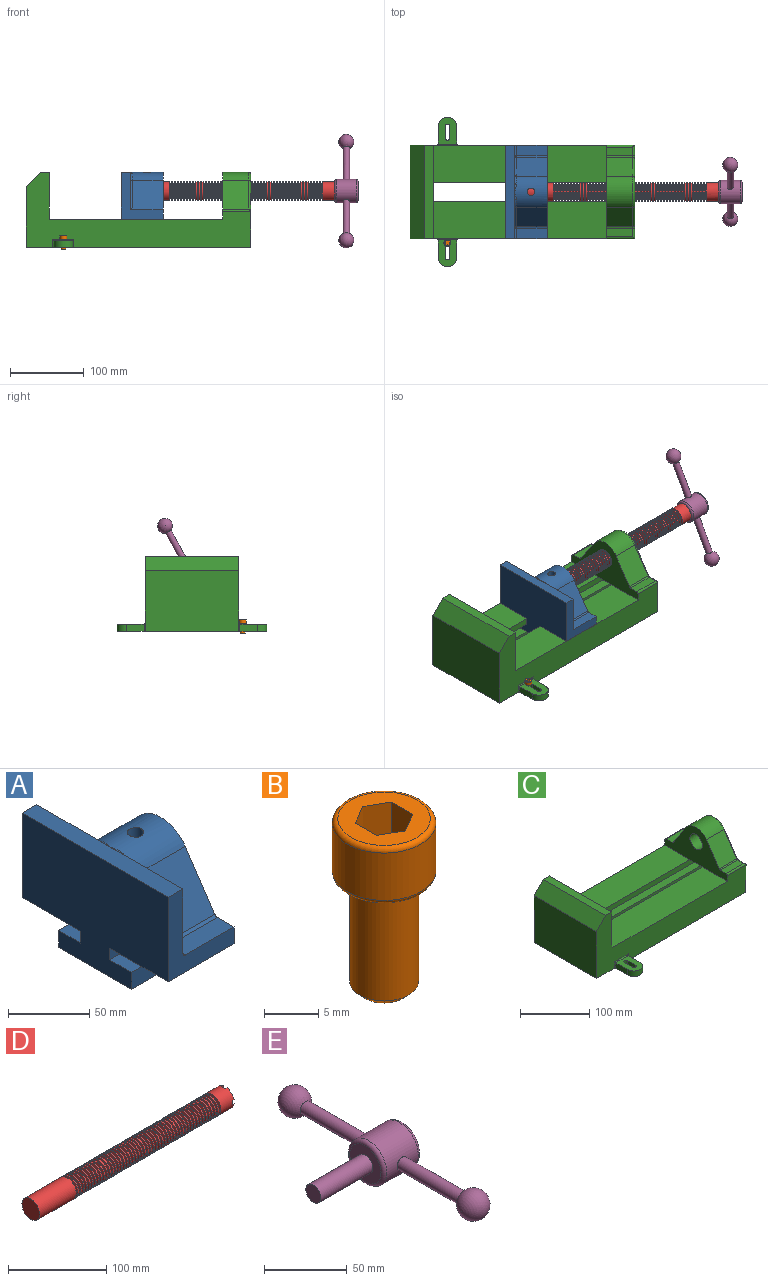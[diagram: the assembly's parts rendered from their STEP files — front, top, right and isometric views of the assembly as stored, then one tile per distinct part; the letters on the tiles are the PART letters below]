
ASSEMBLY  parts=5 mates=5
PART A: 36 faces, bbox 57.2x127x89 mm
  f0: plane 57.15x50.8mm, normal (0,0,-1), area 2903.2mm2, adj f6,f9,f10,f23
  f1: cylinder r=12.7mm len=44.45mm, axis (1,0,0), area 3464.3mm2, adj f6,f15,f16
  f2: plane 41.91x14.52mm, normal (0,0,1), area 608.5mm2, adj f6,f11,f24,f25
  f3: plane 51.86x48.26mm, normal (1,0,0), area 1495.7mm2, adj f8,f10,f31,f33,f35
  f4: plane 51.86x48.26mm, normal (1,0,0), area 1495.7mm2, adj f8,f11,f24,f28,f29
  f5: plane 57.15x50.8mm, normal (0,0,-1), area 2903.2mm2, adj f6,f9,f11,f22
  f6: plane 127x85.09mm, normal (1,0,0), area 5190.6mm2, adj f0,f1,f2,f5,f7,f10,f11,f12
  f7: plane 41.91x14.52mm, normal (0,0,1), area 608.5mm2, adj f6,f10,f30,f31
  f8: plane 127x12.7mm, normal (0,0,1), area 1612.9mm2, adj f3,f4,f9,f10,f11,f26,f34
  f9: plane 127x85.09mm, normal (-1,0,0), area 9096.8mm2, adj f0,f5,f8,f10,f11,f17,f18,f19
  f10: plane 63.5x57.15mm, normal (0,-1,0), area 1372.3mm2, adj f0,f3,f6,f7,f8,f9,f31
  f11: plane 63.5x57.15mm, normal (0,1,0), area 1372.3mm2, adj f2,f4,f5,f6,f8,f9,f24
  f12: plane 41.91x38.43mm, normal (0,-0.83,0.56), area 1939.2mm2, adj f6,f13,f30,f33
  f13: cylinder r=25.4mm len=44.45mm, axis (1,0,0), area 2026.5mm2, adj f6,f12,f14,f16,f26,f28,f34,f35
  f14: plane 41.91x38.43mm, normal (0,0.83,0.56), area 1939.2mm2, adj f6,f13,f25,f29
  f15: plane 25.4x25.4mm, normal (1,0,0), area 506.7mm2, adj f1
  f16: cylinder r=5.08mm len=13.76mm, axis (0,0,1), area 414mm2, adj f1,f13
  f17: plane 57.15x19.05mm, normal (0,0,1), area 1088.7mm2, adj f6,f9,f18,f23
  f18: plane 57.15x12.7mm, normal (0,-1,0), area 725.8mm2, adj f6,f9,f17,f19
  f19: plane 63.5x57.15mm, normal (0,0,-1), area 3629mm2, adj f6,f9,f18,f20
  f20: plane 57.15x12.7mm, normal (0,1,0), area 725.8mm2, adj f6,f9,f19,f21
  f21: plane 57.15x19.05mm, normal (0,0,1), area 1088.7mm2, adj f6,f9,f20,f22
  f22: plane 57.15x8.89mm, normal (0,1,0), area 508.1mm2, adj f5,f6,f9,f21
  f23: plane 57.15x8.89mm, normal (0,-1,0), area 508.1mm2, adj f0,f6,f9,f17
  f24: cylinder r=2.54mm len=14.52mm, axis (0,-1,0), area 57.9mm2, adj f2,f4,f11,f27
  f25: cylinder r=2.54mm len=41.91mm, axis (1,0,0), area 104.3mm2, adj f2,f6,f14,f27
  f26: bspline ~12.24x2.8mm, area 20.9mm2, adj f8,f13,f28
  f27: sphere r=2.54mm, area 6.3mm2, adj f24,f25,f29
  f28: torus R=27.94mm, axis (1,0,0), area 57.8mm2, adj f4,f13,f26,f29
  f29: cylinder r=2.54mm len=39.84mm, axis (0,-0.56,0.83), area 184.6mm2, adj f4,f14,f27,f28
  f30: cylinder r=2.54mm len=41.91mm, axis (1,0,0), area 104.3mm2, adj f6,f7,f12,f32
  f31: cylinder r=2.54mm len=14.52mm, axis (0,-1,0), area 57.9mm2, adj f3,f7,f10,f32
  f32: sphere r=2.54mm, area 6.3mm2, adj f30,f31,f33
  f33: cylinder r=2.54mm len=39.84mm, axis (0,-0.56,-0.83), area 184.6mm2, adj f3,f12,f32,f35
  f34: bspline ~12.24x2.8mm, area 20.9mm2, adj f8,f13,f35
  f35: torus R=27.94mm, axis (1,0,0), area 57.8mm2, adj f3,f13,f33,f34
PART B: 15 faces, bbox 10.3x10.3x19.1 mm
  f0: plane 8.51x8.51mm, normal (0,0,1), area 37.2mm2, adj f5,f6,f7,f8,f9,f10,f14
  f1: cylinder r=3.17mm len=11.94mm, axis (0,0,1), area 238.2mm2, adj f4,f12
  f2: plane 4.83x4.83mm, normal (0,0,-1), area 18.3mm2, adj f12
  f3: cylinder r=4.76mm len=9.53mm, axis (0,0,-1), area 159.6mm2, adj f13,f14
  f4: plane 8.51x8.51mm, normal (0,0,-1), area 25.2mm2, adj f1,f13
  f5: plane 4.83x2.38mm, normal (-0.5,-0.87,0), area 13.3mm2, adj f0,f6,f10,f11
  f6: plane 4.83x2.38mm, normal (0.5,-0.87,0), area 13.3mm2, adj f0,f5,f7,f11
  f7: plane 4.83x2.75mm, normal (1,0,0), area 13.3mm2, adj f0,f6,f8,f11
  f8: plane 4.83x2.38mm, normal (0.5,0.87,0), area 13.3mm2, adj f0,f7,f9,f11
  f9: plane 4.83x2.38mm, normal (-0.5,0.87,0), area 13.3mm2, adj f0,f8,f10,f11
  f10: plane 4.83x2.75mm, normal (-1,0,0), area 13.3mm2, adj f0,f5,f9,f11
  f11: plane 5.5x4.76mm, normal (0,0,1), area 19.6mm2, adj f5,f6,f7,f8,f9,f10
  f12: cone r=3.17mm half-angle=45deg, axis (0,0,1), area 18.9mm2, adj f1,f2
  f13: torus R=4.25mm, axis (0,0,1), area 23mm2, adj f3,f4
  f14: torus R=4.25mm, axis (0,0,1), area 23mm2, adj f0,f3
PART C: 61 faces, bbox 304.8x203.2x103.7 mm
  f0: plane 304.8x101.6mm, normal (0,1,0), area 13520.3mm2, adj f3,f4,f5,f6,f7,f8,f9,f16
  f1: plane 304.8x101.6mm, normal (0,-1,0), area 13520.3mm2, adj f2,f3,f5,f6,f7,f8,f9,f16
  f2: plane 234.95x50.8mm, normal (0,0,1), area 11935.5mm2, adj f1,f5,f16,f26
  f3: plane 127x99.06mm, normal (1,0,0), area 7097.5mm2, adj f0,f1,f9,f14,f17,f18,f19,f20
  f4: plane 234.95x50.8mm, normal (0,0,1), area 11935.5mm2, adj f0,f5,f16,f27
  f5: plane 127x101.6mm, normal (1,0,0), area 9516.1mm2, adj f0,f1,f2,f4,f6,f9,f18,f19
  f6: plane 127x12.7mm, normal (0,0,1), area 1612.9mm2, adj f0,f1,f5,f7
  f7: plane 127x19.05mm, normal (-0.71,0,0.71), area 3421.5mm2, adj f0,f1,f6,f8
  f8: plane 127x82.55mm, normal (-1,0,0), area 10483.8mm2, adj f0,f1,f7,f9
  f9: plane 304.8x203.2mm, normal (0,0,-1), area 33298.3mm2, adj f0,f1,f3,f5,f8,f21,f22,f39
  f10: plane 35.56x11.98mm, normal (0,0,1), area 426mm2, adj f16,f28,f29,f30
  f11: plane 38.43x35.56mm, normal (0,0.83,0.56), area 1645.4mm2, adj f12,f16,f29,f32
  f12: cylinder r=25.4mm len=42.19mm, axis (1,0,0), area 1770.2mm2, adj f11,f13,f16,f33
  f13: plane 38.43x35.56mm, normal (0,-0.83,0.56), area 1645.4mm2, adj f12,f16,f34,f35
  f14: cylinder r=12.7mm len=38.1mm, axis (1,0,0), area 3040.2mm2, adj f3,f16
  f15: plane 35.56x11.98mm, normal (0,0,1), area 426mm2, adj f16,f34,f36,f38
  f16: plane 127x63.5mm, normal (-1,0,0), area 4155.5mm2, adj f0,f1,f2,f4,f10,f11,f12,f13
  f17: plane 38.1x25.4mm, normal (0,0,-1), area 967.7mm2, adj f3,f16,f26,f27
  f18: plane 273.05x19.05mm, normal (0,0,-1), area 5201.6mm2, adj f3,f5,f19,f26
  f19: plane 273.05x12.7mm, normal (0,1,0), area 3467.7mm2, adj f3,f5,f18,f20
  f20: plane 273.05x19.05mm, normal (0,0,1), area 5201.6mm2, adj f3,f5,f19,f21
  f21: plane 273.05x16.51mm, normal (0,1,0), area 4508.1mm2, adj f3,f5,f9,f20
  f22: plane 273.05x16.51mm, normal (0,-1,0), area 4508.1mm2, adj f3,f5,f9,f23
  f23: plane 273.05x19.05mm, normal (0,0,1), area 5201.6mm2, adj f3,f5,f22,f24
  f24: plane 273.05x12.7mm, normal (0,-1,0), area 3467.7mm2, adj f3,f5,f23,f25
  f25: plane 273.05x19.05mm, normal (0,0,-1), area 5201.6mm2, adj f3,f5,f24,f27
  f26: plane 273.05x8.89mm, normal (0,1,0), area 2427.4mm2, adj f2,f3,f5,f17,f18
  f27: plane 273.05x8.89mm, normal (0,-1,0), area 2427.4mm2, adj f3,f4,f5,f17,f25
  f28: cylinder r=2.54mm len=38.1mm, axis (1,0,0), area 148.3mm2, adj f0,f10,f16,f30
  f29: cylinder r=2.54mm len=35.56mm, axis (-1,0,0), area 88.5mm2, adj f10,f11,f16,f31
  f30: cylinder r=2.54mm len=14.52mm, axis (0,1,0), area 54.3mm2, adj f3,f10,f28,f31
  f31: torus R=5.08mm, axis (-1,0,0), area 13.5mm2, adj f3,f29,f30,f32
  f32: cylinder r=2.54mm len=39.84mm, axis (0,0.56,-0.83), area 184.6mm2, adj f3,f11,f31,f33
  f33: torus R=22.86mm, axis (-1,0,0), area 191.4mm2, adj f3,f12,f32,f35
  f34: cylinder r=2.54mm len=35.56mm, axis (-1,0,0), area 88.5mm2, adj f13,f15,f16,f37
  f35: cylinder r=2.54mm len=39.84mm, axis (0,0.56,0.83), area 184.6mm2, adj f3,f13,f33,f37
  f36: cylinder r=2.54mm len=38.1mm, axis (-1,0,0), area 148.3mm2, adj f1,f15,f16,f38
  f37: torus R=5.08mm, axis (-1,0,0), area 13.5mm2, adj f3,f34,f35,f38
  f38: cylinder r=2.54mm len=14.52mm, axis (0,1,0), area 54.3mm2, adj f3,f15,f36,f37
  f39: plane 23.88x9.53mm, normal (-1,0,0), area 227.4mm2, adj f9,f45,f46,f60
  f40: plane 23.88x9.53mm, normal (1,0,0), area 227.4mm2, adj f9,f45,f46,f58
  f41: cylinder r=3.3mm len=9.53mm, axis (0,0,-1), area 98.8mm2, adj f9,f42,f44,f46
  f42: plane 15.62x9.53mm, normal (-1,0,0), area 148.8mm2, adj f9,f41,f43,f46
  f43: cylinder r=3.3mm len=9.53mm, axis (0,0,-1), area 98.8mm2, adj f9,f42,f44,f46
  f44: plane 15.62x9.53mm, normal (1,0,0), area 148.8mm2, adj f9,f41,f43,f46
  f45: cylinder r=12.7mm len=25.4mm, axis (0,0,-1), area 380mm2, adj f9,f39,f40,f46
  f46: plane 36.58x25.4mm, normal (0,0,1), area 722.4mm2, adj f39,f40,f41,f42,f43,f44,f45,f59
  f47: plane 23.88x9.53mm, normal (-1,0,0), area 227.4mm2, adj f9,f53,f54,f56
  f48: plane 23.88x9.53mm, normal (1,0,0), area 227.4mm2, adj f9,f53,f54,f55
  f49: cylinder r=3.3mm len=9.53mm, axis (0,0,-1), area 98.8mm2, adj f9,f50,f52,f54
  f50: plane 15.62x9.53mm, normal (-1,0,0), area 148.8mm2, adj f9,f49,f51,f54
  f51: cylinder r=3.3mm len=9.53mm, axis (0,0,-1), area 98.8mm2, adj f9,f50,f52,f54
  f52: plane 15.62x9.53mm, normal (1,0,0), area 148.8mm2, adj f9,f49,f51,f54
  f53: cylinder r=12.7mm len=25.4mm, axis (0,0,-1), area 380mm2, adj f9,f47,f48,f54
  f54: plane 36.58x25.4mm, normal (0,0,1), area 722.4mm2, adj f47,f48,f49,f50,f51,f52,f53,f57
  f55: cylinder r=1.52mm len=11.05mm, axis (0,0,-1), area 24.1mm2, adj f0,f9,f48,f57
  f56: cylinder r=1.52mm len=11.05mm, axis (0,0,1), area 24.1mm2, adj f0,f9,f47,f57
  f57: cylinder r=1.52mm len=28.45mm, axis (1,0,0), area 63.5mm2, adj f0,f54,f55,f56
  f58: cylinder r=1.52mm len=11.05mm, axis (0,0,1), area 24.1mm2, adj f1,f9,f40,f59
  f59: cylinder r=1.52mm len=28.45mm, axis (-1,0,0), area 63.5mm2, adj f1,f46,f58,f60
  f60: cylinder r=1.52mm len=11.05mm, axis (0,0,-1), area 24.1mm2, adj f1,f9,f39,f59
PART D: 220 faces, bbox 279.4x25.4x25.4 mm
  f0: cylinder r=12.7mm len=25.4mm, axis (-1,0,0), area 1468.2mm2, adj f1,f2,f3,f5,f7,f208,f209,f210
  f1: plane 9.9x9.9mm, normal (1,0,0), area 62.3mm2, adj f0,f4,f213,f216
  f2: plane 9.9x9.9mm, normal (1,0,0), area 62.3mm2, adj f0,f4,f210,f218
  f3: plane 9.9x9.9mm, normal (1,0,0), area 62.3mm2, adj f0,f4,f209,f212
  f4: cylinder r=6.35mm len=25.4mm, axis (1,0,0), area 960.3mm2, adj f1,f2,f3,f5,f6,f208,f209,f210
  f5: plane 9.9x9.9mm, normal (1,0,0), area 62.3mm2, adj f0,f4,f215,f217
  f6: plane 12.7x12.7mm, normal (1,0,0), area 126.7mm2, adj f4
  f7: cone r=12.7mm half-angle=76deg, axis (1,0,0), area 188mm2, adj f0,f9
  f8: cone r=10.16mm half-angle=76deg, axis (-1,0,0), area 188mm2, adj f9,f10
  f9: cylinder r=10.16mm len=20.32mm, axis (1,0,0), area 81.1mm2, adj f7,f8
  f10: cylinder r=12.7mm len=25.4mm, axis (-1,0,0), area 131.7mm2, adj f8,f11
  f11: cone r=12.7mm half-angle=76deg, axis (1,0,0), area 188mm2, adj f10,f13
  f12: cone r=10.16mm half-angle=76deg, axis (-1,0,0), area 188mm2, adj f13,f14
  f13: cylinder r=10.16mm len=20.32mm, axis (1,0,0), area 81.1mm2, adj f11,f12
  f14: cylinder r=12.7mm len=25.4mm, axis (-1,0,0), area 131.7mm2, adj f12,f15
  f15: cone r=12.7mm half-angle=76deg, axis (1,0,0), area 188mm2, adj f14,f17
  f16: cone r=10.16mm half-angle=76deg, axis (-1,0,0), area 188mm2, adj f17,f18
  f17: cylinder r=10.16mm len=20.32mm, axis (1,0,0), area 81.1mm2, adj f15,f16
  f18: cylinder r=12.7mm len=25.4mm, axis (-1,0,0), area 131.7mm2, adj f16,f19
  f19: cone r=12.7mm half-angle=76deg, axis (1,0,0), area 188mm2, adj f18,f21
  f20: cone r=10.16mm half-angle=76deg, axis (-1,0,0), area 188mm2, adj f21,f22
  f21: cylinder r=10.16mm len=20.32mm, axis (1,0,0), area 81.1mm2, adj f19,f20
  f22: cylinder r=12.7mm len=25.4mm, axis (-1,0,0), area 131.7mm2, adj f20,f23
  f23: cone r=12.7mm half-angle=76deg, axis (1,0,0), area 188mm2, adj f22,f25
  f24: cone r=10.16mm half-angle=76deg, axis (-1,0,0), area 188mm2, adj f25,f26
  f25: cylinder r=10.16mm len=20.32mm, axis (1,0,0), area 81.1mm2, adj f23,f24
  f26: cylinder r=12.7mm len=25.4mm, axis (-1,0,0), area 131.7mm2, adj f24,f27
  f27: cone r=12.7mm half-angle=76deg, axis (1,0,0), area 188mm2, adj f26,f29
  f28: cone r=10.16mm half-angle=76deg, axis (-1,0,0), area 188mm2, adj f29,f30
  f29: cylinder r=10.16mm len=20.32mm, axis (1,0,0), area 81.1mm2, adj f27,f28
  f30: cylinder r=12.7mm len=25.4mm, axis (-1,0,0), area 131.7mm2, adj f28,f31
  f31: cone r=12.7mm half-angle=76deg, axis (1,0,0), area 188mm2, adj f30,f33
  f32: cone r=10.16mm half-angle=76deg, axis (-1,0,0), area 188mm2, adj f33,f34
  f33: cylinder r=10.16mm len=20.32mm, axis (1,0,0), area 81.1mm2, adj f31,f32
  f34: cylinder r=12.7mm len=25.4mm, axis (-1,0,0), area 131.7mm2, adj f32,f35
  f35: cone r=12.7mm half-angle=76deg, axis (1,0,0), area 188mm2, adj f34,f37
  f36: cone r=10.16mm half-angle=76deg, axis (-1,0,0), area 188mm2, adj f37,f38
  f37: cylinder r=10.16mm len=20.32mm, axis (1,0,0), area 81.1mm2, adj f35,f36
  f38: cylinder r=12.7mm len=25.4mm, axis (-1,0,0), area 131.7mm2, adj f36,f39
  f39: cone r=12.7mm half-angle=76deg, axis (1,0,0), area 188mm2, adj f38,f41
  f40: cone r=10.16mm half-angle=76deg, axis (-1,0,0), area 188mm2, adj f41,f42
  f41: cylinder r=10.16mm len=20.32mm, axis (1,0,0), area 81.1mm2, adj f39,f40
  f42: cylinder r=12.7mm len=25.4mm, axis (-1,0,0), area 131.7mm2, adj f40,f43
  f43: cone r=12.7mm half-angle=76deg, axis (1,0,0), area 188mm2, adj f42,f45
  f44: cone r=10.16mm half-angle=76deg, axis (-1,0,0), area 188mm2, adj f45,f46
  f45: cylinder r=10.16mm len=20.32mm, axis (1,0,0), area 81.1mm2, adj f43,f44
  f46: cylinder r=12.7mm len=25.4mm, axis (-1,0,0), area 131.7mm2, adj f44,f47
  f47: cone r=12.7mm half-angle=76deg, axis (1,0,0), area 188mm2, adj f46,f49
  f48: cone r=10.16mm half-angle=76deg, axis (-1,0,0), area 188mm2, adj f49,f50
  f49: cylinder r=10.16mm len=20.32mm, axis (1,0,0), area 81.1mm2, adj f47,f48
  f50: cylinder r=12.7mm len=25.4mm, axis (-1,0,0), area 131.7mm2, adj f48,f51
  f51: cone r=12.7mm half-angle=76deg, axis (1,0,0), area 188mm2, adj f50,f53
  f52: cone r=10.16mm half-angle=76deg, axis (-1,0,0), area 188mm2, adj f53,f54
  f53: cylinder r=10.16mm len=20.32mm, axis (1,0,0), area 81.1mm2, adj f51,f52
  f54: cylinder r=12.7mm len=25.4mm, axis (-1,0,0), area 131.7mm2, adj f52,f55
  f55: cone r=12.7mm half-angle=76deg, axis (1,0,0), area 188mm2, adj f54,f57
  f56: cone r=10.16mm half-angle=76deg, axis (-1,0,0), area 188mm2, adj f57,f58
  f57: cylinder r=10.16mm len=20.32mm, axis (1,0,0), area 81.1mm2, adj f55,f56
  f58: cylinder r=12.7mm len=25.4mm, axis (-1,0,0), area 131.7mm2, adj f56,f59
  f59: cone r=12.7mm half-angle=76deg, axis (1,0,0), area 188mm2, adj f58,f61
  f60: cone r=10.16mm half-angle=76deg, axis (-1,0,0), area 188mm2, adj f61,f62
  f61: cylinder r=10.16mm len=20.32mm, axis (1,0,0), area 81.1mm2, adj f59,f60
  f62: cylinder r=12.7mm len=25.4mm, axis (-1,0,0), area 131.7mm2, adj f60,f63
  f63: cone r=12.7mm half-angle=76deg, axis (1,0,0), area 188mm2, adj f62,f65
  f64: cone r=10.16mm half-angle=76deg, axis (-1,0,0), area 188mm2, adj f65,f66
  f65: cylinder r=10.16mm len=20.32mm, axis (1,0,0), area 81.1mm2, adj f63,f64
  f66: cylinder r=12.7mm len=25.4mm, axis (-1,0,0), area 131.7mm2, adj f64,f67
  f67: cone r=12.7mm half-angle=76deg, axis (1,0,0), area 188mm2, adj f66,f69
  f68: cone r=10.16mm half-angle=76deg, axis (-1,0,0), area 188mm2, adj f69,f70
  f69: cylinder r=10.16mm len=20.32mm, axis (1,0,0), area 81.1mm2, adj f67,f68
  f70: cylinder r=12.7mm len=25.4mm, axis (-1,0,0), area 131.7mm2, adj f68,f71
  f71: cone r=12.7mm half-angle=76deg, axis (1,0,0), area 188mm2, adj f70,f73
  f72: cone r=10.16mm half-angle=76deg, axis (-1,0,0), area 188mm2, adj f73,f74
  f73: cylinder r=10.16mm len=20.32mm, axis (1,0,0), area 81.1mm2, adj f71,f72
  f74: cylinder r=12.7mm len=25.4mm, axis (-1,0,0), area 131.7mm2, adj f72,f75
  f75: cone r=12.7mm half-angle=76deg, axis (1,0,0), area 188mm2, adj f74,f77
  f76: cone r=10.16mm half-angle=76deg, axis (-1,0,0), area 188mm2, adj f77,f78
  f77: cylinder r=10.16mm len=20.32mm, axis (1,0,0), area 81.1mm2, adj f75,f76
  f78: cylinder r=12.7mm len=25.4mm, axis (-1,0,0), area 131.7mm2, adj f76,f79
  f79: cone r=12.7mm half-angle=76deg, axis (1,0,0), area 188mm2, adj f78,f81
  f80: cone r=10.16mm half-angle=76deg, axis (-1,0,0), area 188mm2, adj f81,f82
  f81: cylinder r=10.16mm len=20.32mm, axis (1,0,0), area 81.1mm2, adj f79,f80
  f82: cylinder r=12.7mm len=25.4mm, axis (-1,0,0), area 131.7mm2, adj f80,f83
  f83: cone r=12.7mm half-angle=76deg, axis (1,0,0), area 188mm2, adj f82,f85
  f84: cone r=10.16mm half-angle=76deg, axis (-1,0,0), area 188mm2, adj f85,f86
  f85: cylinder r=10.16mm len=20.32mm, axis (1,0,0), area 81.1mm2, adj f83,f84
  f86: cylinder r=12.7mm len=25.4mm, axis (-1,0,0), area 131.7mm2, adj f84,f87
  f87: cone r=12.7mm half-angle=76deg, axis (1,0,0), area 188mm2, adj f86,f89
  f88: cone r=10.16mm half-angle=76deg, axis (-1,0,0), area 188mm2, adj f89,f90
  f89: cylinder r=10.16mm len=20.32mm, axis (1,0,0), area 81.1mm2, adj f87,f88
  f90: cylinder r=12.7mm len=25.4mm, axis (-1,0,0), area 131.7mm2, adj f88,f91
  f91: cone r=12.7mm half-angle=76deg, axis (1,0,0), area 188mm2, adj f90,f93
  f92: cone r=10.16mm half-angle=76deg, axis (-1,0,0), area 188mm2, adj f93,f94
  f93: cylinder r=10.16mm len=20.32mm, axis (1,0,0), area 81.1mm2, adj f91,f92
  f94: cylinder r=12.7mm len=25.4mm, axis (-1,0,0), area 131.7mm2, adj f92,f95
  f95: cone r=12.7mm half-angle=76deg, axis (1,0,0), area 188mm2, adj f94,f97
  f96: cone r=10.16mm half-angle=76deg, axis (-1,0,0), area 188mm2, adj f97,f98
  f97: cylinder r=10.16mm len=20.32mm, axis (1,0,0), area 81.1mm2, adj f95,f96
  f98: cylinder r=12.7mm len=25.4mm, axis (-1,0,0), area 131.7mm2, adj f96,f99
  f99: cone r=12.7mm half-angle=76deg, axis (1,0,0), area 188mm2, adj f98,f101
  f100: cone r=10.16mm half-angle=76deg, axis (-1,0,0), area 188mm2, adj f101,f102
  f101: cylinder r=10.16mm len=20.32mm, axis (1,0,0), area 81.1mm2, adj f99,f100
  f102: cylinder r=12.7mm len=25.4mm, axis (-1,0,0), area 131.7mm2, adj f100,f103
  f103: cone r=12.7mm half-angle=76deg, axis (1,0,0), area 188mm2, adj f102,f105
  f104: cone r=10.16mm half-angle=76deg, axis (-1,0,0), area 188mm2, adj f105,f106
  f105: cylinder r=10.16mm len=20.32mm, axis (1,0,0), area 81.1mm2, adj f103,f104
  f106: cylinder r=12.7mm len=25.4mm, axis (-1,0,0), area 131.7mm2, adj f104,f107
  f107: cone r=12.7mm half-angle=76deg, axis (1,0,0), area 188mm2, adj f106,f109
  f108: cone r=10.16mm half-angle=76deg, axis (-1,0,0), area 188mm2, adj f109,f110
  f109: cylinder r=10.16mm len=20.32mm, axis (1,0,0), area 81.1mm2, adj f107,f108
  f110: cylinder r=12.7mm len=25.4mm, axis (-1,0,0), area 131.7mm2, adj f108,f111
  f111: cone r=12.7mm half-angle=76deg, axis (1,0,0), area 188mm2, adj f110,f113
  f112: cone r=10.16mm half-angle=76deg, axis (-1,0,0), area 188mm2, adj f113,f114
  f113: cylinder r=10.16mm len=20.32mm, axis (1,0,0), area 81.1mm2, adj f111,f112
  f114: cylinder r=12.7mm len=25.4mm, axis (-1,0,0), area 131.7mm2, adj f112,f115
  f115: cone r=12.7mm half-angle=76deg, axis (1,0,0), area 188mm2, adj f114,f117
  f116: cone r=10.16mm half-angle=76deg, axis (-1,0,0), area 188mm2, adj f117,f118
  f117: cylinder r=10.16mm len=20.32mm, axis (1,0,0), area 81.1mm2, adj f115,f116
  f118: cylinder r=12.7mm len=25.4mm, axis (-1,0,0), area 131.7mm2, adj f116,f119
  f119: cone r=12.7mm half-angle=76deg, axis (1,0,0), area 188mm2, adj f118,f121
  f120: cone r=10.16mm half-angle=76deg, axis (-1,0,0), area 188mm2, adj f121,f122
  f121: cylinder r=10.16mm len=20.32mm, axis (1,0,0), area 81.1mm2, adj f119,f120
  f122: cylinder r=12.7mm len=25.4mm, axis (-1,0,0), area 131.7mm2, adj f120,f123
  f123: cone r=12.7mm half-angle=76deg, axis (1,0,0), area 188mm2, adj f122,f125
  f124: cone r=10.16mm half-angle=76deg, axis (-1,0,0), area 188mm2, adj f125,f126
  f125: cylinder r=10.16mm len=20.32mm, axis (1,0,0), area 81.1mm2, adj f123,f124
  f126: cylinder r=12.7mm len=25.4mm, axis (-1,0,0), area 131.7mm2, adj f124,f127
  f127: cone r=12.7mm half-angle=76deg, axis (1,0,0), area 188mm2, adj f126,f129
  f128: cone r=10.16mm half-angle=76deg, axis (-1,0,0), area 188mm2, adj f129,f130
  f129: cylinder r=10.16mm len=20.32mm, axis (1,0,0), area 81.1mm2, adj f127,f128
  f130: cylinder r=12.7mm len=25.4mm, axis (-1,0,0), area 131.7mm2, adj f128,f131
  f131: cone r=12.7mm half-angle=76deg, axis (1,0,0), area 188mm2, adj f130,f133
  f132: cone r=10.16mm half-angle=76deg, axis (-1,0,0), area 188mm2, adj f133,f134
  f133: cylinder r=10.16mm len=20.32mm, axis (1,0,0), area 81.1mm2, adj f131,f132
  f134: cylinder r=12.7mm len=25.4mm, axis (-1,0,0), area 131.7mm2, adj f132,f135
  f135: cone r=12.7mm half-angle=76deg, axis (1,0,0), area 188mm2, adj f134,f137
  f136: cone r=10.16mm half-angle=76deg, axis (-1,0,0), area 188mm2, adj f137,f138
  f137: cylinder r=10.16mm len=20.32mm, axis (1,0,0), area 81.1mm2, adj f135,f136
  f138: cylinder r=12.7mm len=25.4mm, axis (-1,0,0), area 131.7mm2, adj f136,f139
  f139: cone r=12.7mm half-angle=76deg, axis (1,0,0), area 188mm2, adj f138,f141
  f140: cone r=10.16mm half-angle=76deg, axis (-1,0,0), area 188mm2, adj f141,f142
  f141: cylinder r=10.16mm len=20.32mm, axis (1,0,0), area 81.1mm2, adj f139,f140
  f142: cylinder r=12.7mm len=25.4mm, axis (-1,0,0), area 131.7mm2, adj f140,f143
  f143: cone r=12.7mm half-angle=76deg, axis (1,0,0), area 188mm2, adj f142,f145
  f144: cone r=10.16mm half-angle=76deg, axis (-1,0,0), area 188mm2, adj f145,f146
  f145: cylinder r=10.16mm len=20.32mm, axis (1,0,0), area 81.1mm2, adj f143,f144
  f146: cylinder r=12.7mm len=25.4mm, axis (-1,0,0), area 131.7mm2, adj f144,f147
  f147: cone r=12.7mm half-angle=76deg, axis (1,0,0), area 188mm2, adj f146,f149
  f148: cone r=10.16mm half-angle=76deg, axis (-1,0,0), area 188mm2, adj f149,f150
  f149: cylinder r=10.16mm len=20.32mm, axis (1,0,0), area 81.1mm2, adj f147,f148
  f150: cylinder r=12.7mm len=25.4mm, axis (-1,0,0), area 131.7mm2, adj f148,f151
  f151: cone r=12.7mm half-angle=76deg, axis (1,0,0), area 188mm2, adj f150,f153
  f152: cone r=10.16mm half-angle=76deg, axis (-1,0,0), area 188mm2, adj f153,f154
  f153: cylinder r=10.16mm len=20.32mm, axis (1,0,0), area 81.1mm2, adj f151,f152
  f154: cylinder r=12.7mm len=25.4mm, axis (-1,0,0), area 131.7mm2, adj f152,f155
  f155: cone r=12.7mm half-angle=76deg, axis (1,0,0), area 188mm2, adj f154,f157
  f156: cone r=10.16mm half-angle=76deg, axis (-1,0,0), area 188mm2, adj f157,f158
  f157: cylinder r=10.16mm len=20.32mm, axis (1,0,0), area 81.1mm2, adj f155,f156
  f158: cylinder r=12.7mm len=25.4mm, axis (-1,0,0), area 131.7mm2, adj f156,f159
  f159: cone r=12.7mm half-angle=76deg, axis (1,0,0), area 188mm2, adj f158,f161
  f160: cone r=10.16mm half-angle=76deg, axis (-1,0,0), area 188mm2, adj f161,f162
  f161: cylinder r=10.16mm len=20.32mm, axis (1,0,0), area 81.1mm2, adj f159,f160
  f162: cylinder r=12.7mm len=25.4mm, axis (-1,0,0), area 131.7mm2, adj f160,f163
  f163: cone r=12.7mm half-angle=76deg, axis (1,0,0), area 188mm2, adj f162,f165
  f164: cone r=10.16mm half-angle=76deg, axis (-1,0,0), area 188mm2, adj f165,f166
  f165: cylinder r=10.16mm len=20.32mm, axis (1,0,0), area 81.1mm2, adj f163,f164
  f166: cylinder r=12.7mm len=25.4mm, axis (-1,0,0), area 131.7mm2, adj f164,f167
  f167: cone r=12.7mm half-angle=76deg, axis (1,0,0), area 188mm2, adj f166,f169
  f168: cone r=10.16mm half-angle=76deg, axis (-1,0,0), area 188mm2, adj f169,f170
  f169: cylinder r=10.16mm len=20.32mm, axis (1,0,0), area 81.1mm2, adj f167,f168
  f170: cylinder r=12.7mm len=25.4mm, axis (-1,0,0), area 131.7mm2, adj f168,f171
  f171: cone r=12.7mm half-angle=76deg, axis (1,0,0), area 188mm2, adj f170,f173
  f172: cone r=10.16mm half-angle=76deg, axis (-1,0,0), area 188mm2, adj f173,f174
  f173: cylinder r=10.16mm len=20.32mm, axis (1,0,0), area 81.1mm2, adj f171,f172
  f174: cylinder r=12.7mm len=25.4mm, axis (-1,0,0), area 131.7mm2, adj f172,f175
  f175: cone r=12.7mm half-angle=76deg, axis (1,0,0), area 188mm2, adj f174,f177
  f176: cone r=10.16mm half-angle=76deg, axis (-1,0,0), area 188mm2, adj f177,f178
  f177: cylinder r=10.16mm len=20.32mm, axis (1,0,0), area 81.1mm2, adj f175,f176
  f178: cylinder r=12.7mm len=25.4mm, axis (-1,0,0), area 131.7mm2, adj f176,f179
  f179: cone r=12.7mm half-angle=76deg, axis (1,0,0), area 188mm2, adj f178,f181
  f180: cone r=10.16mm half-angle=76deg, axis (-1,0,0), area 188mm2, adj f181,f182
  f181: cylinder r=10.16mm len=20.32mm, axis (1,0,0), area 81.1mm2, adj f179,f180
  f182: cylinder r=12.7mm len=25.4mm, axis (-1,0,0), area 131.7mm2, adj f180,f183
  f183: cone r=12.7mm half-angle=76deg, axis (1,0,0), area 188mm2, adj f182,f185
  f184: cone r=10.16mm half-angle=76deg, axis (-1,0,0), area 188mm2, adj f185,f186
  f185: cylinder r=10.16mm len=20.32mm, axis (1,0,0), area 81.1mm2, adj f183,f184
  f186: cylinder r=12.7mm len=25.4mm, axis (-1,0,0), area 131.7mm2, adj f184,f187
  f187: cone r=12.7mm half-angle=76deg, axis (1,0,0), area 188mm2, adj f186,f189
  f188: cone r=10.16mm half-angle=76deg, axis (-1,0,0), area 188mm2, adj f189,f190
  f189: cylinder r=10.16mm len=20.32mm, axis (1,0,0), area 81.1mm2, adj f187,f188
  f190: cylinder r=12.7mm len=25.4mm, axis (-1,0,0), area 131.7mm2, adj f188,f191
  f191: cone r=12.7mm half-angle=76deg, axis (1,0,0), area 188mm2, adj f190,f193
  f192: cone r=10.16mm half-angle=76deg, axis (-1,0,0), area 188mm2, adj f193,f194
  f193: cylinder r=10.16mm len=20.32mm, axis (1,0,0), area 81.1mm2, adj f191,f192
  f194: cylinder r=12.7mm len=25.4mm, axis (-1,0,0), area 131.7mm2, adj f192,f195
  f195: cone r=12.7mm half-angle=76deg, axis (1,0,0), area 188mm2, adj f194,f197
  f196: cone r=10.16mm half-angle=76deg, axis (-1,0,0), area 188mm2, adj f197,f198
  f197: cylinder r=10.16mm len=20.32mm, axis (1,0,0), area 81.1mm2, adj f195,f196
  f198: cylinder r=12.7mm len=25.4mm, axis (-1,0,0), area 131.7mm2, adj f196,f199
  f199: cone r=12.7mm half-angle=76deg, axis (1,0,0), area 188mm2, adj f198,f201
  f200: cone r=10.16mm half-angle=76deg, axis (-1,0,0), area 188mm2, adj f201,f202
  f201: cylinder r=10.16mm len=20.32mm, axis (1,0,0), area 81.1mm2, adj f199,f200
  f202: cylinder r=12.7mm len=25.4mm, axis (-1,0,0), area 131.7mm2, adj f200,f203
  f203: cone r=12.7mm half-angle=76deg, axis (1,0,0), area 188mm2, adj f202,f205
  f204: cone r=10.16mm half-angle=76deg, axis (-1,0,0), area 188mm2, adj f205,f207
  f205: cylinder r=10.16mm len=20.32mm, axis (1,0,0), area 81.1mm2, adj f203,f204
  f206: plane 25.4x25.4mm, normal (-1,0,0), area 506.7mm2, adj f207
  f207: cylinder r=12.7mm len=52.45mm, axis (-1,0,0), area 4185.4mm2, adj f204,f206
  f208: plane 6.88x5.08mm, normal (1,0,0), area 32.7mm2, adj f0,f4,f209,f210
  f209: plane 6.62x2.54mm, normal (0,-1,0), area 16.8mm2, adj f0,f3,f4,f208
  f210: plane 6.62x2.54mm, normal (0,1,0), area 16.8mm2, adj f0,f2,f4,f208
  f211: plane 6.88x5.08mm, normal (1,0,0), area 32.7mm2, adj f0,f4,f212,f213
  f212: plane 6.62x2.54mm, normal (0,0,1), area 16.8mm2, adj f0,f3,f4,f211
  f213: plane 6.62x2.54mm, normal (0,0,-1), area 16.8mm2, adj f0,f1,f4,f211
  f214: plane 6.88x5.08mm, normal (1,0,0), area 32.7mm2, adj f0,f4,f215,f216
  f215: plane 6.62x2.54mm, normal (0,1,0), area 16.8mm2, adj f0,f4,f5,f214
  f216: plane 6.62x2.54mm, normal (0,-1,0), area 16.8mm2, adj f0,f1,f4,f214
  f217: plane 6.62x2.54mm, normal (0,0,-1), area 16.8mm2, adj f0,f4,f5,f219
  f218: plane 6.62x2.54mm, normal (0,0,1), area 16.8mm2, adj f0,f2,f4,f219
  f219: plane 6.88x5.08mm, normal (1,0,0), area 32.7mm2, adj f0,f4,f217,f218
PART E: 11 faces, bbox 76.2x172.7x34.4 mm
  f0: sphere r=10.16mm, area 1231.8mm2, adj f1
  f1: cylinder r=4.45mm len=51.82mm, axis (0,1,0), area 1438.5mm2, adj f0,f4
  f2: sphere r=10.16mm, area 1231.8mm2, adj f3
  f3: cylinder r=4.45mm len=51.82mm, axis (0,1,0), area 1438.5mm2, adj f2,f4
  f4: cylinder r=15.88mm len=31.75mm, axis (-1,0,0), area 2534.7mm2, adj f1,f3,f9,f10
  f5: cylinder r=6.35mm len=44.45mm, axis (-1,0,0), area 1773.5mm2, adj f6,f8
  f6: plane 12.7x12.7mm, normal (-1,0,0), area 126.7mm2, adj f5
  f7: plane 26.67x26.67mm, normal (1,0,0), area 558.6mm2, adj f10
  f8: plane 26.67x26.67mm, normal (-1,0,0), area 432mm2, adj f5,f9
  f9: torus R=13.33mm, axis (1,0,0), area 374.8mm2, adj f4,f8
  f10: torus R=13.33mm, axis (1,0,0), area 374.8mm2, adj f4,f7
PLACE A t=(97.41,0,0)mm
PLACE B rot(axis=(0,0,1),53.3deg) t=(-254,-68.96,9.53)mm
PLACE C at identity fixed
PLACE D rot(axis=(1,0,0),61.3deg) t=(97.41,66.85,39.63)mm
PLACE E rot(axis=(1,0,0),61.3deg) t=(75.82,66.85,39.63)mm
MATE planar A.f0 <-> C.f2  axis (0,0,-1) through (-147.06,-38.1,38.1)mm
MATE fastened D.f4 <-> E.f5  axis (1,0,0) through (113.92,0,76.2)mm
MATE pin_slot B.f1 <-> C.f41  axis (0,0,1) through (-254,-68.96,9.52)mm
MATE revolute D.f7 <-> A.f28  axis (-1,0,0) through (-162.94,0,76.2)mm
MATE cylindrical C.f12 <-> D.f7  axis (-1,0,0) through (-38.1,0,76.2)mm
